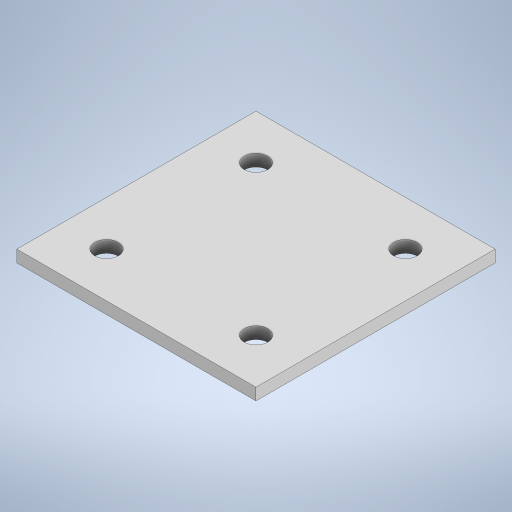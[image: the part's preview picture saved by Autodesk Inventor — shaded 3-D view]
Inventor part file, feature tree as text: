
AUTODESK INVENTOR PART (.ipt)
format: ipt  version: 2024 (Build 280153000, 153)  size: 218,624 bytes
history: native  units: in
note: dims shown in document units (in); Inventor stores cm internally (conversion verified against a paired STEP export)
features: extrude x1, sketch x1
ambient origin geometry x8: Origin, YZ Plane, XZ Plane, XY Plane, X Axis, Y Axis, Z Axis, Center Point
bodies: Solid1 (feature_tree)
feature tree (2):
  extrude  "Extrusion1"  Depth=2.0in
  sketch  "Sketch1"  dims[d0=2.0in d1=2.0in d2=1.25in d3=1.25in d4=0.1969in d5=0.1969in d6=0.1969in d7=0.1969in d8=0.1in d9=0.0in]
